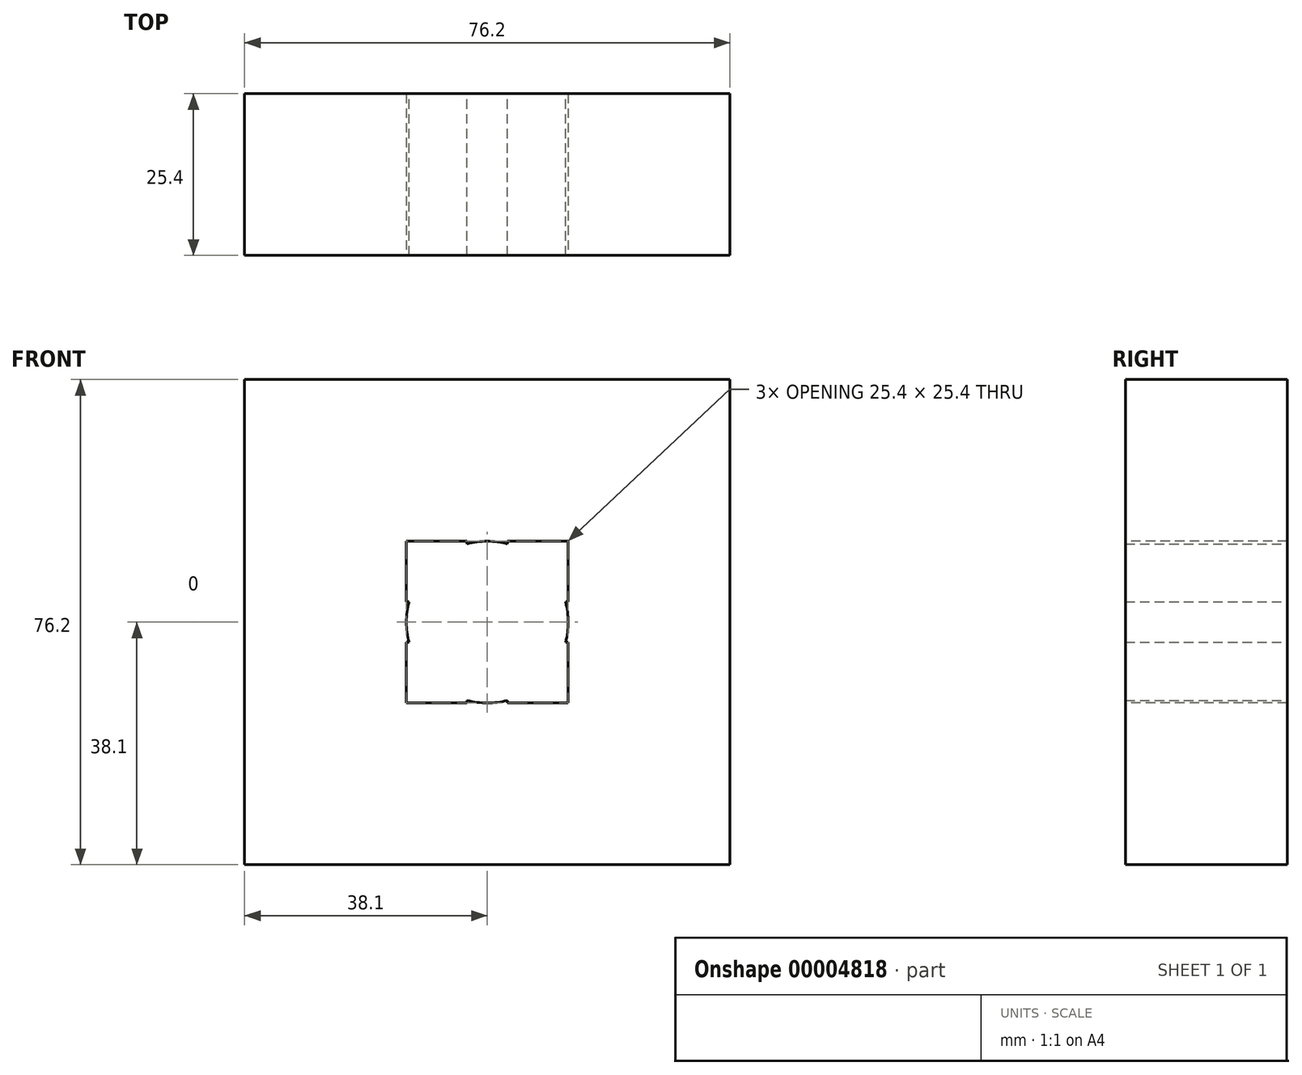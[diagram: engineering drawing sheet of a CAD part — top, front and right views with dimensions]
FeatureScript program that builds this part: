
annotation { "Feature Type Name" : "Feature", "Feature Type Description" : "" }
export const myFeature = defineFeature(function(context is Context, id is Id, definition is map)
    precondition{}
    {
        {
            var Q0;
            Q0=qCreatedBy(makeId("Front.planeOp"),FACE);
            var sketch = newSketch(context, id + "F0", { "sketchPlane" : qUnion([Q0])});
            skLineSegment(sketch, "E0.bottom", {"start": v(-38.1, 76.2) * mm, "end": v(38.1, 76.2) * mm});
            skLineSegment(sketch, "E0.top", {"start": v(-38.1, 0) * mm, "end": v(38.1, 0) * mm});
            skLineSegment(sketch, "E0.left", {"start": v(-38.1, 76.2) * mm, "end": v(-38.1, 0) * mm});
            skLineSegment(sketch, "E0.right", {"start": v(38.1, 76.2) * mm, "end": v(38.1, 0) * mm});
            skSolve(sketch);
        }
        {
            var Q0;
            Q0=qCreatedBy(makeId("Front.planeOp"),FACE);
            var sketch = newSketch(context, id + "F1", { "sketchPlane" : qUnion([Q0])});
            skCircle(sketch, "E1", {"center": v(7.94, 46.04) * mm, "radius": 4.76 * mm});
            skCircle(sketch, "E2", {"center": v(7.94, 30.16) * mm, "radius": 4.76 * mm});
            skCircle(sketch, "E3", {"center": v(-7.94, 30.16) * mm, "radius": 4.76 * mm});
            skCircle(sketch, "E4", {"center": v(-7.94, 46.04) * mm, "radius": 4.76 * mm});
            skSolve(sketch);
        }
        {
            var Q0;
            Q0=qCreatedBy(makeId("Front.planeOp"),FACE);
            var sketch = newSketch(context, id + "F2", { "sketchPlane" : qUnion([Q0])});
            skLineSegment(sketch, "E5.bottom", {"start": v(-12.7, 50.8) * mm, "end": v(-3.18, 50.8) * mm});
            skLineSegment(sketch, "E5.top", {"start": v(-12.7, 41.28) * mm, "end": v(-3.18, 41.28) * mm});
            skLineSegment(sketch, "E5.left", {"start": v(-12.7, 50.8) * mm, "end": v(-12.7, 41.27) * mm});
            skLineSegment(sketch, "E5.right", {"start": v(-3.18, 50.8) * mm, "end": v(-3.18, 41.27) * mm});
            skLineSegment(sketch, "E6.bottom", {"start": v(3.17, 50.8) * mm, "end": v(12.7, 50.8) * mm});
            skLineSegment(sketch, "E6.top", {"start": v(3.17, 41.28) * mm, "end": v(12.7, 41.28) * mm});
            skLineSegment(sketch, "E6.left", {"start": v(3.17, 50.8) * mm, "end": v(3.17, 41.27) * mm});
            skLineSegment(sketch, "E6.right", {"start": v(12.7, 50.8) * mm, "end": v(12.7, 41.27) * mm});
            skLineSegment(sketch, "E7.bottom", {"start": v(-12.7, 34.93) * mm, "end": v(-3.18, 34.93) * mm});
            skLineSegment(sketch, "E7.top", {"start": v(-12.7, 25.4) * mm, "end": v(-3.18, 25.4) * mm});
            skLineSegment(sketch, "E7.left", {"start": v(-12.7, 34.92) * mm, "end": v(-12.7, 25.4) * mm});
            skLineSegment(sketch, "E7.right", {"start": v(-3.18, 34.92) * mm, "end": v(-3.18, 25.4) * mm});
            skLineSegment(sketch, "E8.bottom", {"start": v(3.17, 34.93) * mm, "end": v(12.7, 34.93) * mm});
            skLineSegment(sketch, "E8.top", {"start": v(3.17, 25.4) * mm, "end": v(12.7, 25.4) * mm});
            skLineSegment(sketch, "E8.left", {"start": v(3.17, 34.92) * mm, "end": v(3.17, 25.4) * mm});
            skLineSegment(sketch, "E8.right", {"start": v(12.7, 34.92) * mm, "end": v(12.7, 25.4) * mm});
            skSolve(sketch);
        }
        {
            var Q0;
            Q0=qCreatedBy(makeId("Front.planeOp"),FACE);
            var sketch = newSketch(context, id + "F3", { "sketchPlane" : qUnion([Q0])});
            skCircle(sketch, "E9", {"center": v(0, 38.1) * mm, "radius": 12.7 * mm});
            skSolve(sketch);
        }
        {
            var Q0;
            Q0 = qSketchRegion(id + "F0", true);
            extrude(context, id + "F4", {"entities" : qUnion([Q0]), "endBound" : BoundingType.SYMMETRIC, "depth" : 25.4 * mm, "offsetDistance" : 25.4 * mm});
        }
        {
            var Q0;
            Q0 = qSketchRegion(id + "F1", true);
            extrude(context, id + "F5", {"entities" : qUnion([Q0]), "operationType" : NewBodyOperationType.REMOVE, "endBound" : BoundingType.SYMMETRIC, "depth" : 25.4 * mm, "offsetDistance" : 25.4 * mm});
        }
        {
            var Q0;
            Q0 = qSketchRegion(id + "F0", true);
            extrude(context, id + "F6", {"entities" : qUnion([Q0]), "endBound" : BoundingType.SYMMETRIC, "depth" : 25.4 * mm, "offsetDistance" : 25.4 * mm});
        }
        {
            var Q0;
            Q0 = qSketchRegion(id + "F2", true);
            extrude(context, id + "F7", {"entities" : qUnion([Q0]), "operationType" : NewBodyOperationType.REMOVE, "endBound" : BoundingType.SYMMETRIC, "oppositeDirection" : true, "depth" : 25.4 * mm, "offsetDistance" : 25.4 * mm});
        }
        {
            var Q0;
            Q0 = qSketchRegion(id + "F0", true);
            extrude(context, id + "F8", {"entities" : qUnion([Q0]), "endBound" : BoundingType.SYMMETRIC, "depth" : 25.4 * mm, "offsetDistance" : 25.4 * mm});
        }
        {
            var Q0;
            Q0 = qSketchRegion(id + "F2", true);
            extrude(context, id + "F9", {"entities" : qUnion([Q0]), "operationType" : NewBodyOperationType.REMOVE, "endBound" : BoundingType.SYMMETRIC, "depth" : 25.4 * mm, "offsetDistance" : 25.4 * mm});
        }
        {
            var Q0;
            Q0 = qSketchRegion(id + "F3", true);
            extrude(context, id + "F10", {"entities" : qUnion([Q0]), "operationType" : NewBodyOperationType.REMOVE, "endBound" : BoundingType.SYMMETRIC, "depth" : 25.4 * mm, "offsetDistance" : 25.4 * mm});
        }
    });
